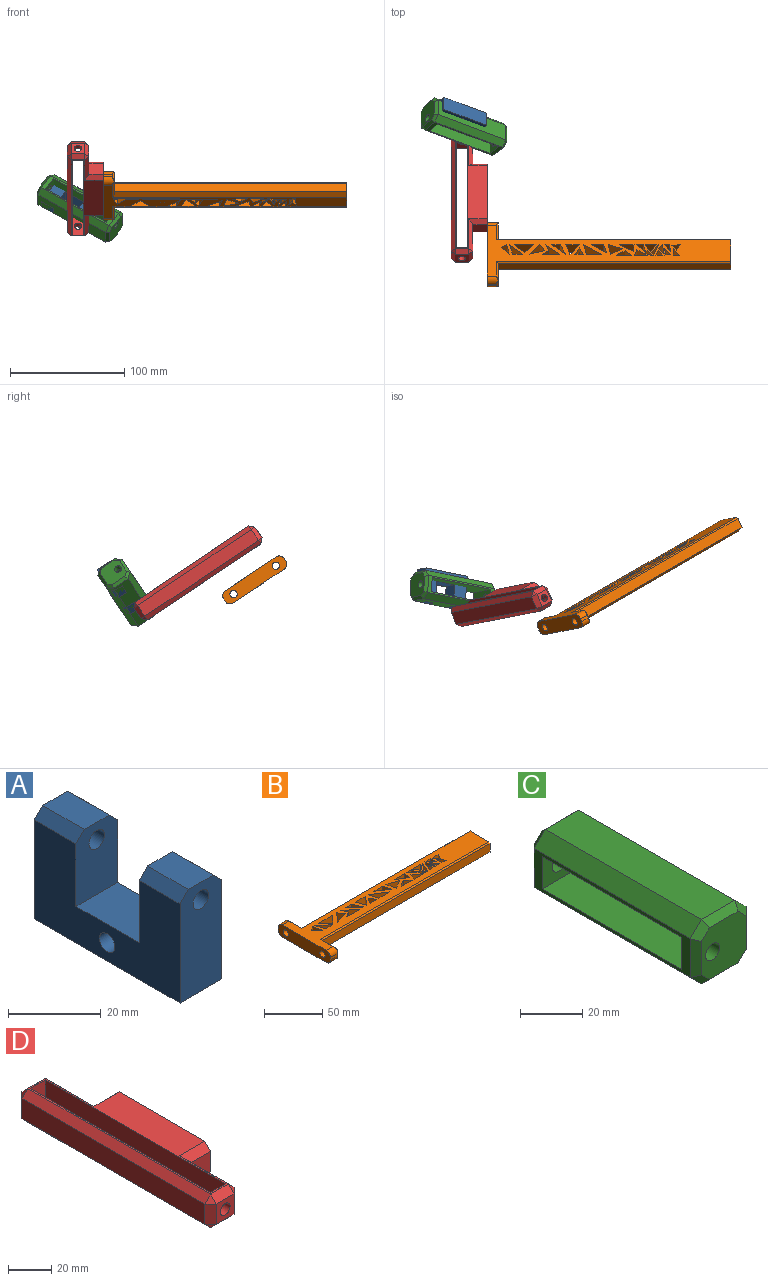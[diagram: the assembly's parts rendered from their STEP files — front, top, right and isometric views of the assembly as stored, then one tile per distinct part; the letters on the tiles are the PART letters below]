
ASSEMBLY  parts=4 mates=4
PART A: 17 faces, bbox 12.7x44.5x28.7 mm
  f0: plane 19.3x12.7mm, normal (0,0,1), area 245.2mm2, adj f3,f4,f7,f9
  f1: plane 44.45x12.7mm, normal (0,0,-1), area 564.5mm2, adj f3,f4,f5,f6
  f2: cylinder r=2.37mm len=12.7mm, axis (-1,0,0), area 189.5mm2, adj f3,f4
  f3: plane 44.45x26.16mm, normal (1,0,0), area 826.5mm2, adj f0,f1,f2,f5,f6,f7,f9,f11
  f4: plane 44.45x26.16mm, normal (-1,0,0), area 826.5mm2, adj f0,f1,f2,f5,f6,f7,f9,f12
  f5: plane 28.7x12.7mm, normal (0,-1,0), area 340.3mm2, adj f1,f3,f4,f8,f11,f12,f16
  f6: plane 28.7x12.7mm, normal (0,1,0), area 340.3mm2, adj f1,f3,f4,f10,f13,f14,f15
  f7: plane 19.05x12.7mm, normal (0,1,0), area 217.8mm2, adj f0,f3,f4,f8,f11,f12,f16
  f8: plane 12.45x7.62mm, normal (0,0,1), area 94.8mm2, adj f5,f7,f11,f12
  f9: plane 19.05x12.7mm, normal (0,-1,0), area 217.8mm2, adj f0,f3,f4,f10,f13,f14,f15
  f10: plane 12.7x7.62mm, normal (0,0,1), area 96.8mm2, adj f6,f9,f13,f14
  f11: plane 12.45x2.54mm, normal (0.71,0,0.71), area 44.7mm2, adj f3,f5,f7,f8
  f12: plane 12.45x2.54mm, normal (-0.71,0,0.71), area 44.7mm2, adj f4,f5,f7,f8
  f13: plane 12.7x2.54mm, normal (-0.71,0,0.71), area 45.6mm2, adj f4,f6,f9,f10
  f14: plane 12.7x2.54mm, normal (0.71,0,0.71), area 45.6mm2, adj f3,f6,f9,f10
  f15: cylinder r=2.37mm len=12.7mm, axis (0,1,0), area 189.5mm2, adj f6,f9
  f16: cylinder r=2.37mm len=12.45mm, axis (0,1,0), area 185.7mm2, adj f5,f7
PART B: 101 faces, bbox 212.6x63.5x12.7 mm
  f0: plane 212.6x53.34mm, normal (0,0,1), area 4264.9mm2, adj f4,f8,f12,f13,f16,f17,f22,f23
  f1: plane 212.6x53.34mm, normal (0,0,-1), area 2187.4mm2, adj f4,f8,f15,f19,f24,f25,f26,f27
  f2: plane 21.06x10.16mm, normal (1,0,0), area 120.6mm2, adj f3,f17,f18,f19,f21,f22,f25,f27
  f3: plane 203.2x8.8mm, normal (0,-1,0), area 1788.1mm2, adj f2,f4,f16,f27
  f4: plane 25.4x12.7mm, normal (1,0,0), area 304.3mm2, adj f0,f1,f3,f5,f12,f16,f26,f27
  f5: plane 203.2x8.8mm, normal (0,1,0), area 1788.1mm2, adj f4,f6,f12,f26
  f6: plane 21.06x10.16mm, normal (1,0,0), area 120.6mm2, adj f5,f13,f14,f15,f20,f23,f24,f26
  f7: plane 8.13x2.54mm, normal (0,1,0), area 20.6mm2, adj f8,f14,f23,f24
  f8: plane 63.5x12.7mm, normal (-1,0,0), area 721mm2, adj f0,f1,f7,f9,f10,f11,f22,f23
  f9: plane 8.13x2.54mm, normal (0,-1,0), area 20.6mm2, adj f8,f18,f22,f25
  f10: cylinder r=3.17mm len=8.13mm, axis (1,0,0), area 162.1mm2, adj f8,f21
  f11: cylinder r=3.17mm len=8.13mm, axis (1,0,0), area 162.1mm2, adj f8,f20
  f12: plane 204.47x1.27mm, normal (0,0.71,0.71), area 366.1mm2, adj f0,f4,f5,f13
  f13: plane 18.6x1.27mm, normal (0.71,0,0.71), area 30.4mm2, adj f0,f6,f12,f23
  f14: plane 9.26x1.27mm, normal (0.71,0.71,0), area 12.8mm2, adj f6,f7,f23,f24
  f15: plane 23.68x1.27mm, normal (0.71,0,-0.71), area 37.9mm2, adj f1,f6,f24,f26
  f16: plane 204.47x1.27mm, normal (0,-0.71,0.71), area 366.1mm2, adj f0,f3,f4,f17
  f17: plane 18.6x1.27mm, normal (0.71,0,0.71), area 30.4mm2, adj f0,f2,f16,f22
  f18: plane 9.26x1.27mm, normal (0.71,-0.71,0), area 12.8mm2, adj f2,f9,f22,f25
  f19: plane 23.68x1.27mm, normal (0.71,0,-0.71), area 37.9mm2, adj f1,f2,f25,f27
  f20: cone r=3.17mm half-angle=45deg, axis (1,0,0), area 43mm2, adj f6,f11
  f21: cone r=3.17mm half-angle=45deg, axis (1,0,0), area 43mm2, adj f2,f10
  f22: cylinder r=5.08mm len=9.4mm, axis (-1,0,0), area 68.8mm2, adj f0,f2,f8,f9,f17,f18
  f23: cylinder r=5.08mm len=9.4mm, axis (1,0,0), area 68.8mm2, adj f0,f6,f7,f8,f13,f14
  f24: cylinder r=5.08mm len=9.4mm, axis (-1,0,0), area 68.8mm2, adj f1,f6,f7,f8,f14,f15
  f25: cylinder r=5.08mm len=9.4mm, axis (1,0,0), area 68.8mm2, adj f1,f2,f8,f9,f18,f19
  f26: plane 204.47x6.35mm, normal (0,0.38,-0.92), area 1398.7mm2, adj f1,f4,f5,f6,f15,f38,f81,f84
  f27: plane 204.47x6.35mm, normal (0,-0.38,-0.92), area 1398.7mm2, adj f1,f2,f3,f4,f19
  f28: plane 12.7x7.08mm, normal (0.71,0.71,0), area 127.2mm2, adj f0,f1,f29,f30
  f29: plane 12.7x4.79mm, normal (0.52,-0.85,0), area 71.1mm2, adj f0,f1,f28,f30
  f30: plane 12.7x9.99mm, normal (-0.97,-0.22,0), area 130.2mm2, adj f0,f1,f28,f29
  f31: plane 13.46x12.7mm, normal (-0.26,0.97,0), area 177.1mm2, adj f0,f1,f32,f33
  f32: plane 12.7x9.99mm, normal (0.73,-0.69,0), area 174.6mm2, adj f0,f1,f31,f33
  f33: plane 12.7x6.35mm, normal (-0.84,-0.53,0), area 95.4mm2, adj f0,f1,f31,f32
  f34: plane 12.7x8.42mm, normal (0,1,0), area 107mm2, adj f0,f1,f35,f36
  f35: plane 12.7x9.99mm, normal (0.96,0.29,0), area 132.7mm2, adj f0,f1,f34,f36
  f36: plane 12.7x11.49mm, normal (-0.66,-0.75,0), area 193.3mm2, adj f0,f1,f34,f35
  f37: plane 12.7x8.62mm, normal (0.7,0.71,0), area 153.3mm2, adj f0,f1,f38,f39
  f38: plane 16.91x12.7mm, normal (0,-1,0), area 214.8mm2, adj f0,f26,f37,f39
  f39: plane 12.7x8.46mm, normal (-0.71,0.7,0), area 150.5mm2, adj f0,f1,f37,f38
  f40: plane 12.7x6.35mm, normal (0.93,0.36,0), area 86.6mm2, adj f0,f1,f41,f43
  f41: plane 12.7x12.25mm, normal (-0.64,-0.77,0), area 202.3mm2, adj f0,f1,f40,f42
  f42: plane 15.12x12.7mm, normal (0,1,0), area 192.1mm2, adj f0,f1,f41,f43
  f43: plane 12.7x5.36mm, normal (0.58,-0.81,0), area 83.7mm2, adj f0,f1,f40,f42
  f44: plane 12.7x4.89mm, normal (0.75,0.66,0), area 82.9mm2, adj f0,f1,f45,f46
  f45: plane 12.7x7.57mm, normal (0.1,-0.99,0), area 96.7mm2, adj f0,f1,f44,f46
  f46: plane 12.7x5.67mm, normal (-0.87,0.5,0), area 83mm2, adj f0,f1,f44,f45
  f47: plane 12.7x5.25mm, normal (0.09,1,0), area 66.9mm2, adj f0,f1,f48,f49
  f48: plane 12.7x6.55mm, normal (1,0,0), area 83.1mm2, adj f0,f1,f47,f49
  f49: plane 12.7x7.01mm, normal (-0.8,-0.6,0), area 111mm2, adj f0,f1,f47,f48
  f50: plane 12.7x10.18mm, normal (0.98,0.21,0), area 132.3mm2, adj f0,f1,f51,f52
  f51: plane 12.7x12.44mm, normal (-0.33,-0.94,0), area 167.5mm2, adj f0,f1,f50,f52
  f52: plane 12.7x10.24mm, normal (-0.49,0.87,0), area 149.6mm2, adj f0,f1,f50,f51
  f53: plane 13.11x12.7mm, normal (0.04,1,0), area 166.7mm2, adj f0,f1,f54,f55
  f54: plane 12.7x7.47mm, normal (0.53,-0.85,0), area 111.5mm2, adj f0,f1,f53,f55
  f55: plane 12.7x5.65mm, normal (-0.67,-0.74,0), area 96.6mm2, adj f0,f1,f53,f54
  f56: plane 12.7x11.44mm, normal (0,1,0), area 145.3mm2, adj f0,f1,f57,f58
  f57: plane 12.7x6.37mm, normal (0.94,-0.34,0), area 86.2mm2, adj f0,f1,f56,f58
  f58: plane 12.7x9.11mm, normal (-0.58,-0.82,0), area 141.6mm2, adj f0,f1,f56,f57
  f59: plane 13.21x12.7mm, normal (0,1,0), area 167.8mm2, adj f0,f1,f60,f61
  f60: plane 12.7x10.18mm, normal (0.96,0.27,0), area 134.3mm2, adj f0,f1,f59,f61
  f61: plane 16.08x12.7mm, normal (-0.53,-0.84,0), area 241.7mm2, adj f0,f1,f59,f60
  f62: plane 12.7x7.47mm, normal (0,1,0), area 94.8mm2, adj f0,f1,f63,f64
  f63: plane 12.7x6.7mm, normal (0.86,-0.51,0), area 99.2mm2, adj f0,f1,f62,f64
  f64: plane 12.7x6.7mm, normal (-0.89,-0.46,0), area 95.7mm2, adj f0,f1,f62,f63
  f65: plane 12.7x5.86mm, normal (0,1,0), area 74.5mm2, adj f0,f1,f66,f67
  f66: plane 12.7x4.56mm, normal (0.89,-0.46,0), area 65.4mm2, adj f0,f1,f65,f67
  f67: plane 12.7x4.56mm, normal (-0.8,-0.61,0), area 72.8mm2, adj f0,f1,f65,f66
  f68: plane 12.7x10.91mm, normal (-0.93,0.36,0), area 148.8mm2, adj f0,f1,f69,f70
  f69: plane 12.7x2.68mm, normal (0.81,0.59,0), area 41.9mm2, adj f0,f1,f68,f70
  f70: plane 12.7x8.24mm, normal (0.8,-0.6,0), area 131mm2, adj f0,f1,f68,f69
  f71: plane 12.7x6.63mm, normal (0.98,0.19,0), area 85.8mm2, adj f0,f1,f72,f73
  f72: plane 12.7x6.65mm, normal (-0.77,-0.64,0), area 109.5mm2, adj f0,f1,f71,f73
  f73: plane 12.7x4.2mm, normal (0,1,0), area 53.3mm2, adj f0,f1,f71,f72
  f74: plane 12.7x10.91mm, normal (-0.98,-0.18,0), area 140.8mm2, adj f0,f1,f75,f76
  f75: plane 12.7x6.55mm, normal (0.8,0.6,0), area 103.6mm2, adj f0,f1,f74,f76
  f76: plane 12.7x4.36mm, normal (0.83,-0.55,0), area 66.6mm2, adj f0,f1,f74,f75
  f77: plane 12.7x3.87mm, normal (1,0,0), area 49.2mm2, adj f0,f1,f78,f79
  f78: plane 12.7x5.98mm, normal (-0.72,-0.69,0), area 105.3mm2, adj f0,f1,f77,f79
  f79: plane 12.7x5.77mm, normal (0.34,0.94,0), area 78mm2, adj f0,f1,f77,f78
  f80: plane 12.7x7.18mm, normal (0.8,0.6,0), area 113.6mm2, adj f0,f1,f81,f82
  f81: plane 12.7x4.54mm, normal (0,-1,0), area 57.6mm2, adj f0,f26,f80,f82
  f82: plane 12.7x7.18mm, normal (-0.99,-0.11,0), area 91.7mm2, adj f0,f1,f80,f81
  f83: plane 13.21x12.7mm, normal (0.55,0.84,0), area 200.5mm2, adj f0,f1,f84,f85
  f84: plane 12.7x10.53mm, normal (0,-1,0), area 133.7mm2, adj f0,f26,f83,f85
  f85: plane 12.7x8.65mm, normal (-0.96,-0.3,0), area 115mm2, adj f0,f1,f83,f84
  f86: plane 12.7x12.06mm, normal (0,-1,0), area 153.2mm2, adj f0,f26,f87,f88
  f87: plane 12.7x10.18mm, normal (-0.78,0.63,0), area 166.3mm2, adj f0,f1,f86,f88
  f88: plane 12.7x10.18mm, normal (0.94,0.35,0), area 138.1mm2, adj f0,f1,f86,f87
  f89: plane 12.7x12.06mm, normal (0.64,0.76,0), area 200.4mm2, adj f0,f1,f90,f91
  f90: plane 12.7x7.47mm, normal (0,-1,0), area 94.8mm2, adj f0,f26,f89,f91
  f91: plane 12.7x10.18mm, normal (-0.91,-0.41,0), area 141.8mm2, adj f0,f1,f89,f90
  f92: plane 12.7x7.14mm, normal (0.85,0.53,0), area 106.7mm2, adj f0,f1,f93,f94
  f93: plane 12.7x10.25mm, normal (0,-1,0), area 130.1mm2, adj f0,f26,f92,f94
  f94: plane 12.7x7.14mm, normal (-0.77,0.63,0), area 117mm2, adj f0,f1,f92,f93
  f95: plane 12.7x7.63mm, normal (0.67,0.74,0), area 130.3mm2, adj f0,f1,f96,f97
  f96: plane 12.7x6.32mm, normal (0,-1,0), area 80.2mm2, adj f0,f26,f95,f97
  f97: plane 12.7x6.86mm, normal (-0.98,-0.19,0), area 88.7mm2, adj f0,f1,f95,f96
  f98: plane 12.7x11.96mm, normal (0.51,0.86,0), area 177.2mm2, adj f0,f1,f99,f100
  f99: plane 12.73x12.7mm, normal (0,-1,0), area 161.7mm2, adj f0,f26,f98,f100
  f100: plane 12.7x7.18mm, normal (-0.99,0.11,0), area 91.7mm2, adj f0,f1,f98,f99
PART C: 32 faces, bbox 25.4x76.2x25.4 mm
  f0: plane 71.12x15.24mm, normal (0,0,1), area 1083.9mm2, adj f12,f15,f19,f25
  f1: plane 20.32x20.32mm, normal (0,-1,0), area 355.4mm2, adj f11,f24,f25,f26,f27,f28,f29,f30
  f2: plane 71.12x15.24mm, normal (0,0,-1), area 1083.9mm2, adj f13,f14,f20,f29
  f3: plane 25.4x12.7mm, normal (0,1,0), area 290.9mm2, adj f4,f6,f8,f9,f11
  f4: plane 63.5x25.4mm, normal (0,0,-1), area 1612.9mm2, adj f3,f5,f8,f9
  f5: plane 25.4x12.7mm, normal (0,-1,0), area 290.9mm2, adj f4,f6,f8,f9,f10
  f6: plane 63.5x25.4mm, normal (0,0,1), area 1612.9mm2, adj f3,f5,f8,f9
  f7: plane 20.32x20.32mm, normal (0,1,0), area 355.4mm2, adj f10,f16,f17,f18,f19,f20,f21,f22
  f8: plane 71.12x15.24mm, normal (1,0,0), area 277.4mm2, adj f3,f4,f5,f6,f14,f15,f16,f27
  f9: plane 71.12x15.24mm, normal (-1,0,0), area 277.4mm2, adj f3,f4,f5,f6,f12,f13,f23,f31
  f10: cylinder r=3.17mm len=6.35mm, axis (0,-1,0), area 126.7mm2, adj f5,f7
  f11: cylinder r=3.17mm len=6.35mm, axis (0,-1,0), area 126.7mm2, adj f1,f3
  f12: plane 71.12x5.08mm, normal (-0.71,0,0.71), area 510.9mm2, adj f0,f9,f21,f24
  f13: plane 71.12x5.08mm, normal (-0.71,0,-0.71), area 510.9mm2, adj f2,f9,f22,f30
  f14: plane 71.12x5.08mm, normal (0.71,0,-0.71), area 510.9mm2, adj f2,f8,f18,f28
  f15: plane 71.12x5.08mm, normal (0.71,0,0.71), area 510.9mm2, adj f0,f8,f17,f26
  f16: plane 15.24x2.54mm, normal (0.71,0.71,0), area 51mm2, adj f7,f8,f17,f18
  f17: plane 6.13x6.13mm, normal (0.5,0.71,0.5), area 22mm2, adj f7,f15,f16,f19
  f18: plane 6.13x6.13mm, normal (0.5,0.71,-0.5), area 22mm2, adj f7,f14,f16,f20
  f19: plane 15.24x2.54mm, normal (0,0.71,0.71), area 51mm2, adj f0,f7,f17,f21
  f20: plane 15.24x2.54mm, normal (0,0.71,-0.71), area 51mm2, adj f2,f7,f18,f22
  f21: plane 6.13x6.13mm, normal (-0.5,0.71,0.5), area 22mm2, adj f7,f12,f19,f23
  f22: plane 6.13x6.13mm, normal (-0.5,0.71,-0.5), area 22mm2, adj f7,f13,f20,f23
  f23: plane 15.24x2.54mm, normal (-0.71,0.71,0), area 51mm2, adj f7,f9,f21,f22
  f24: plane 6.13x6.13mm, normal (-0.5,-0.71,0.5), area 22mm2, adj f1,f12,f25,f31
  f25: plane 15.24x2.54mm, normal (0,-0.71,0.71), area 51mm2, adj f0,f1,f24,f26
  f26: plane 6.13x6.13mm, normal (0.5,-0.71,0.5), area 22mm2, adj f1,f15,f25,f27
  f27: plane 15.24x2.54mm, normal (0.71,-0.71,0), area 51mm2, adj f1,f8,f26,f28
  f28: plane 6.13x6.13mm, normal (0.5,-0.71,-0.5), area 22mm2, adj f1,f14,f27,f29
  f29: plane 15.24x2.54mm, normal (0,-0.71,-0.71), area 51mm2, adj f1,f2,f28,f30
  f30: plane 6.13x6.13mm, normal (-0.5,-0.71,-0.5), area 22mm2, adj f1,f13,f29,f31
  f31: plane 15.24x2.54mm, normal (-0.71,-0.71,0), area 51mm2, adj f1,f9,f24,f30
PART D: 46 faces, bbox 31.8x127x19.1 mm
  f0: plane 27.94x11.43mm, normal (1,0,0), area 319.4mm2, adj f11,f34,f41,f42
  f1: plane 119.38x27.94mm, normal (0,0,1), area 1152.7mm2, adj f7,f8,f9,f10,f15,f22,f24,f30
  f2: plane 119.38x27.94mm, normal (0,0,-1), area 1152.7mm2, adj f7,f8,f9,f10,f15,f20,f21,f26
  f3: plane 119.38x11.43mm, normal (-1,0,0), area 1364.5mm2, adj f31,f32,f39,f40
  f4: plane 11.43x11.43mm, normal (0,-1,0), area 99mm2, adj f18,f25,f26,f30,f31
  f5: plane 27.94x11.43mm, normal (1,0,0), area 319.4mm2, adj f12,f21,f24,f25
  f6: plane 11.43x11.43mm, normal (0,1,0), area 99mm2, adj f19,f33,f40,f41,f45
  f7: plane 19.05x9.65mm, normal (0,-1,0), area 152.1mm2, adj f1,f2,f8,f10,f19
  f8: plane 117.6x19.05mm, normal (1,0,0), area 2240.3mm2, adj f1,f2,f7,f9
  f9: plane 19.05x9.65mm, normal (0,1,0), area 152.1mm2, adj f1,f2,f8,f10,f18
  f10: plane 117.6x19.05mm, normal (-1,0,0), area 2240.3mm2, adj f1,f2,f7,f9
  f11: plane 12.7x11.43mm, normal (0,1,0), area 145.2mm2, adj f0,f15,f29,f38
  f12: plane 12.7x11.43mm, normal (0,-1,0), area 145.2mm2, adj f5,f15,f20,f22
  f13: cylinder r=1.35mm len=12.7mm, axis (-1,0,0), area 107.4mm2, adj f15,f16
  f14: cylinder r=1.35mm len=12.7mm, axis (-1,0,0), area 107.4mm2, adj f15,f17
  f15: plane 63.5x19.05mm, normal (1,0,0), area 1169.3mm2, adj f1,f2,f11,f12,f13,f14,f20,f22
  f16: plane 2.69x2.69mm, normal (1,0,0), area 5.7mm2, adj f13
  f17: plane 2.69x2.69mm, normal (1,0,0), area 5.7mm2, adj f14
  f18: cylinder r=3.17mm len=6.35mm, axis (0,-1,0), area 93.7mm2, adj f4,f9
  f19: cylinder r=3.17mm len=6.35mm, axis (0,-1,0), area 93.7mm2, adj f6,f7
  f20: plane 16.51x3.81mm, normal (0,-0.71,-0.71), area 78.7mm2, adj f2,f12,f15,f21
  f21: plane 31.75x3.81mm, normal (0.71,0,-0.71), area 160.8mm2, adj f2,f5,f20,f23
  f22: plane 16.51x3.81mm, normal (0,-0.71,0.71), area 78.7mm2, adj f1,f12,f15,f24
  f23: plane 3.81x3.81mm, normal (0.58,-0.58,-0.58), area 12.6mm2, adj f21,f25,f26
  f24: plane 31.75x3.81mm, normal (0.71,0,0.71), area 160.8mm2, adj f1,f5,f22,f27
  f25: plane 11.43x3.81mm, normal (0.71,-0.71,0), area 61.6mm2, adj f4,f5,f23,f27
  f26: plane 11.43x3.81mm, normal (0,-0.71,-0.71), area 61.6mm2, adj f2,f4,f23,f28
  f27: plane 3.81x3.81mm, normal (0.58,-0.58,0.58), area 12.6mm2, adj f24,f25,f30
  f28: plane 3.81x3.81mm, normal (-0.58,-0.58,-0.58), area 12.6mm2, adj f26,f31,f32
  f29: plane 16.51x3.81mm, normal (0,0.71,-0.71), area 78.7mm2, adj f2,f11,f15,f34
  f30: plane 11.43x3.81mm, normal (0,-0.71,0.71), area 61.6mm2, adj f1,f4,f27,f35
  f31: plane 11.43x3.81mm, normal (-0.71,-0.71,0), area 61.6mm2, adj f3,f4,f28,f35
  f32: plane 119.38x3.81mm, normal (-0.71,0,-0.71), area 643.2mm2, adj f2,f3,f28,f36
  f33: plane 11.43x3.81mm, normal (0,0.71,-0.71), area 61.6mm2, adj f2,f6,f36,f37
  f34: plane 31.75x3.81mm, normal (0.71,0,-0.71), area 160.8mm2, adj f0,f2,f29,f37
  f35: plane 3.81x3.81mm, normal (-0.58,-0.58,0.58), area 12.6mm2, adj f30,f31,f39
  f36: plane 3.81x3.81mm, normal (-0.58,0.58,-0.58), area 12.6mm2, adj f32,f33,f40
  f37: plane 3.81x3.81mm, normal (0.58,0.58,-0.58), area 12.6mm2, adj f33,f34,f41
  f38: plane 16.51x3.81mm, normal (0,0.71,0.71), area 78.7mm2, adj f1,f11,f15,f42
  f39: plane 119.38x3.81mm, normal (-0.71,0,0.71), area 643.2mm2, adj f1,f3,f35,f43
  f40: plane 11.43x3.81mm, normal (-0.71,0.71,0), area 61.6mm2, adj f3,f6,f36,f43
  f41: plane 11.43x3.81mm, normal (0.71,0.71,0), area 61.6mm2, adj f0,f6,f37,f44
  f42: plane 31.75x3.81mm, normal (0.71,0,0.71), area 160.8mm2, adj f0,f1,f38,f44
  f43: plane 3.81x3.81mm, normal (-0.58,0.58,0.58), area 12.6mm2, adj f39,f40,f45
  f44: plane 3.81x3.81mm, normal (0.58,0.58,0.58), area 12.6mm2, adj f41,f42,f45
  f45: plane 11.43x3.81mm, normal (0,0.71,0.71), area 61.6mm2, adj f1,f6,f43,f44
PLACE A rot(axis=(0.71,0.59,-0.39),180deg) t=(-148.53,82.36,-28.73)mm
PLACE B rot(axis=(-1,0,0),33.8deg) t=(-20.54,-33.84,-28.89)mm
PLACE C rot(axis=(0,0.56,0.83),90deg) t=(-152.06,70.98,-27.47)mm
PLACE D rot(axis=(-1,0,0),33.8deg) t=(-144.24,3.13,-18.12)mm
MATE parallel D.f15 <-> B.f8  axis (1,0,0) through (-131.54,19.21,-17.41)mm
MATE planar C.f4 <-> A.f0  axis (-0.56,-0.46,-0.69) through (-148.53,84.47,-30.14)mm
MATE planar A.f15 <-> C.f10  axis (-0.83,0.31,0.46) through (-182.97,90.76,-27.6)mm
MATE pin_slot A.f2 <-> D.f18  axis (0,-0.83,0.56) through (-153.76,87.53,-20.99)mm
